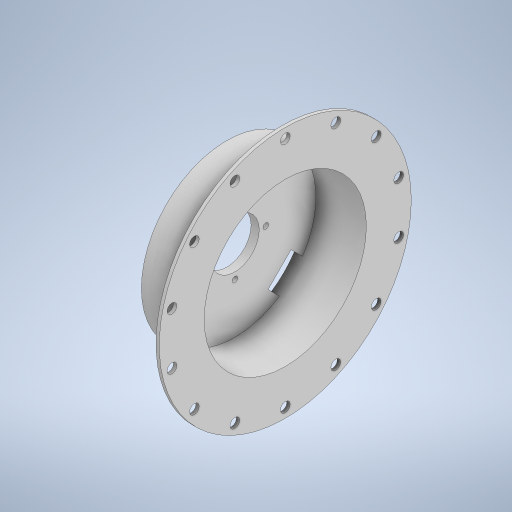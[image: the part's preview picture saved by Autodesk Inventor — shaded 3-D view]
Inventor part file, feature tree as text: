
AUTODESK INVENTOR PART (.ipt)
format: ipt  version: 2023 (Build 270158000, 158)  size: 348,160 bytes
history: native  units: mm
features: extrude x4, sketch x3
ambient origin geometry x8: Origin, YZ Plane, XZ Plane, XY Plane, X Axis, Y Axis, Z Axis, Center Point
bodies: Solid1 (feature_tree)
feature tree (7):
  extrude  "Extrusion1"  Depth=3.5mm
  extrude  "Extrusion2"  Depth=105.0mm
  extrude  "Extrusion4"  Depth=5.0mm TaperAngle=0.0deg
  extrude  "Extrusion6"  Depth=2.0mm
  sketch  "Sketch1"  dims[d0=38.0mm d1=3.5mm]
  sketch  "Sketch2"  dims[d2=40.0mm d4=360.0deg d6=105.0mm]
  sketch  "Sketch6"  dims[d7=80.0mm d8=5.0mm d9=0.0mm d10=105.0mm d11=36.0mm d12=0.0mm d27=30.0mm d28=10.0mm d29=45.0deg d30=10.0mm d31=10.0mm d32=0.0mm d34=10.0mm d35=143.0mm d36=6.0mm d37=70.0mm d39=360.0deg d41=155.0mm d44=140.0mm d46=360.0deg d48=2.0mm d49=0.0mm]
